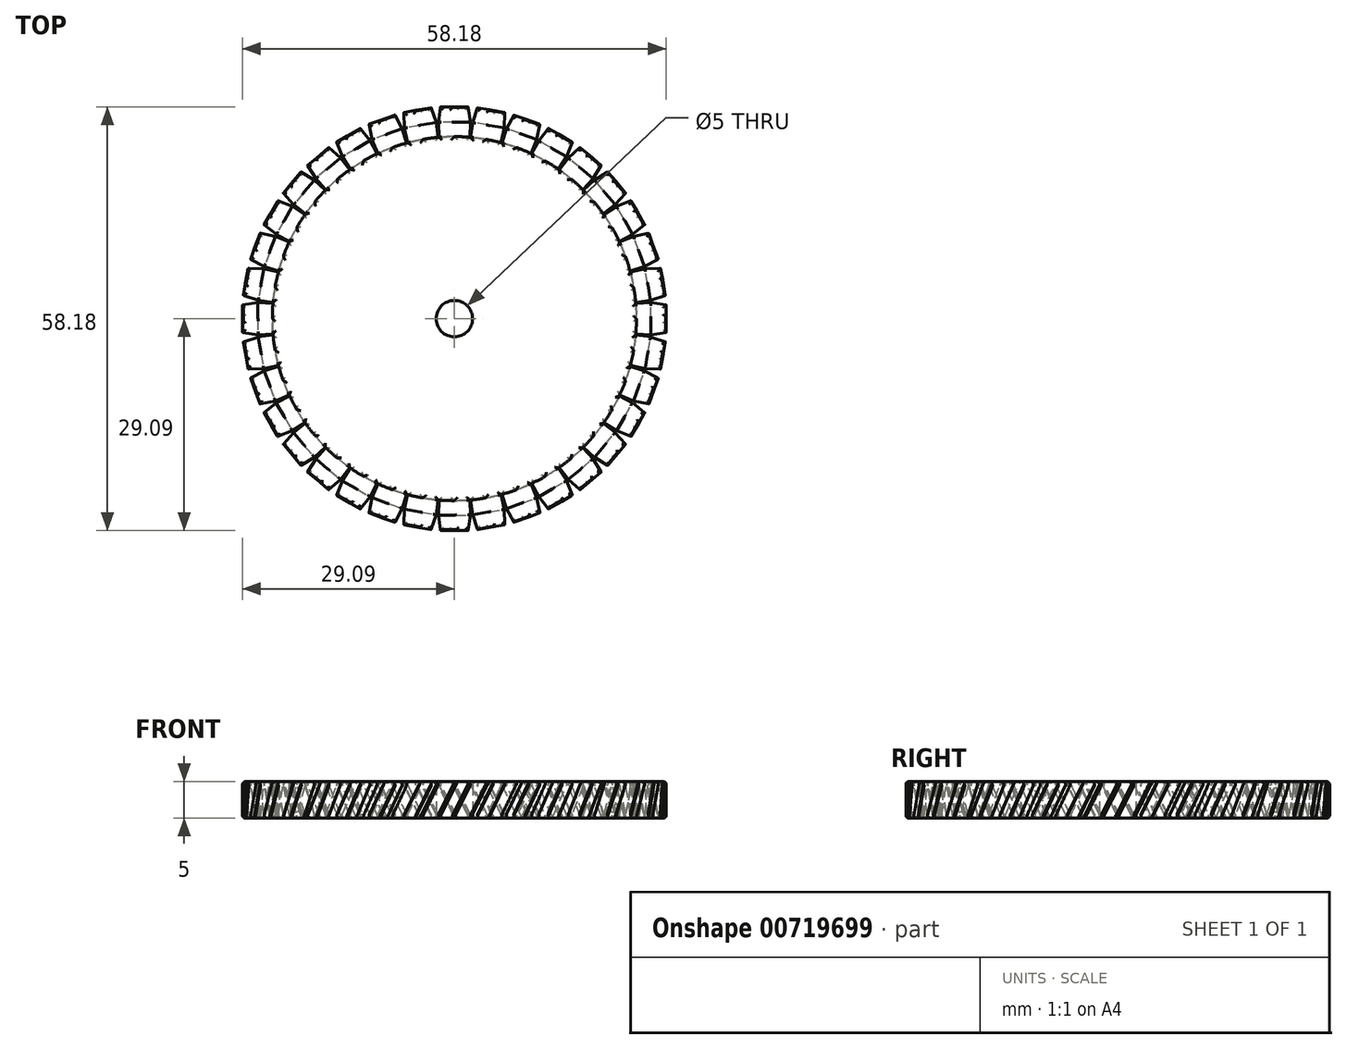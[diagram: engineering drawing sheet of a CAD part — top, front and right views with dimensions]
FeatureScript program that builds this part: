
annotation { "Feature Type Name" : "Feature", "Feature Type Description" : "" }
export const myFeature = defineFeature(function(context is Context, id is Id, definition is map)
    precondition{}
    {
        {
            var Q0;
            Q0=qCreatedBy(makeId("Top.planeOp"),FACE);
            var sketch = newSketch(context, id + "F0", { "sketchPlane" : qUnion([Q0])});
            skCircle(sketch, "E0", {"center": v(0, 0) * mm, "radius": 25 * mm});
            skCircle(sketch, "E1", {"center": v(0, 0) * mm, "radius": 2.5 * mm});
            skSolve(sketch);
        }
        {
            var Q0;
            Q0=makeQuery(id+"F0.imprint","IMPRINT",FACE,{"disambiguationData":[TD([[makeQuery(id+"F0.imprint","IMPRINT",EDGE,{"derivedFrom":sQuery(id+"F0.wireOp",EDGE,"E0")}),1.0]])]});
            extrude(context, id + "F1", {"entities" : qUnion([Q0]), "depth" : 5 * mm, "offsetDistance" : 25 * mm});
        }
        {
            var Q0;
            Q0=qCreatedBy(makeId("Top.planeOp"),FACE);
            cPlane(context, id + "F2", {"entities" : qUnion([Q0]), "cplaneType" : CPlaneType.OFFSET, "offset" : 2.5 * mm, "width" : 150 * mm, "height" : 150 * mm});
        }
        {
            var Q0;
            Q0=qCreatedBy(id+"F2.planeOp",FACE);
            var sketch = newSketch(context, id + "F3", { "sketchPlane" : qUnion([Q0])});
            skCircle(sketch, "E2", {"center": v(0, 0) * mm, "radius": 27 * mm, "construction": true});
            skCircle(sketch, "E3", {"center": v(0, 0) * mm, "radius": 29 * mm, "construction": true});
            skLineSegment(sketch, "E4", {"start": v(-1.1, 24.48) * mm, "end": v(-1.2, 26.97) * mm});
            skLineSegment(sketch, "E5", {"start": v(-1.2, 26.97) * mm, "end": v(-0.9, 28.99) * mm});
            skLineSegment(sketch, "E6", {"start": v(-0.8, 29.09) * mm, "end": v(0.8, 29.09) * mm});
            skLineSegment(sketch, "E7", {"start": v(0.9, 28.99) * mm, "end": v(1.2, 26.97) * mm});
            skLineSegment(sketch, "E8", {"start": v(1.2, 26.97) * mm, "end": v(1.1, 24.48) * mm});
            skLineSegment(sketch, "E9", {"start": v(1.1, 24.48) * mm, "end": v(-1.1, 24.48) * mm});
            skCircle(sketch, "E10", {"center": v(0, 0) * mm, "radius": 24.5 * mm, "construction": true});
            skLineSegment(sketch, "E11", {"start": v(-0.9, 28.99) * mm, "end": v(-0.8, 29.09) * mm});
            skLineSegment(sketch, "E12", {"start": v(0.8, 29.09) * mm, "end": v(0.9, 28.99) * mm});
            skSolve(sketch);
        }
        {
            var Q0;
            Q0=qCreatedBy(makeId("Front.planeOp"),FACE);
            var sketch = newSketch(context, id + "F4", { "sketchPlane" : qUnion([Q0])});
            skLineSegment(sketch, "E13", {"start": v(0, 5) * mm, "end": v(2.5, 0) * mm});
            skSolve(sketch);
        }
        {
            var Q0;
            Q0 = qSketchRegion(id + "F3", true);
            var Q1;
            Q1 = qConstructionFilter(qBodyType(qCreatedBy(id + "F4" ,EDGE), BodyType.WIRE), ConstructionObject.NO);
            sweep(context, id + "F5", {"profiles" : qUnion([Q0]), "path" : qUnion([Q1])});
        }
        {
            var Q0;
            Q0=qCreatedBy(makeId("Front.planeOp"),FACE);
            var sketch = newSketch(context, id + "F6", { "sketchPlane" : qUnion([Q0])});
            skLineSegment(sketch, "E14", {"start": v(0, 7.5) * mm, "end": v(0, -7.5) * mm, "construction": true});
            skSolve(sketch);
        }
        {
            var Q0;
            Q0=makeQuery(id+"F5.opSweep","SWEPT_BODY",BODY,{"disambiguationData":[OSD([sQuery(id+"F3.wireOp",EDGE,"E4"),sQuery(id+"F3.wireOp",EDGE,"E5"),sQuery(id+"F3.wireOp",EDGE,"E6"),sQuery(id+"F3.wireOp",EDGE,"E7"),sQuery(id+"F3.wireOp",EDGE,"E8"),sQuery(id+"F3.wireOp",EDGE,"E9"),sQuery(id+"F4.wireOp",EDGE,"E13")])]});
            var Q1;
            Q1=sQuery(id+"F6.wireOp",EDGE,"E14");
            circularPattern(context, id + "F7", {"entities" : qUnion([Q0]), "axis" : qUnion([Q1]), "angle" : 360 * degree, "instanceCount" : 36, "equalSpace" : true});
        }
        {
            var Q0;
            Q0=makeQuery(id+"F7.opPattern","COPY",BODY,{"derivedFrom":makeQuery(id+"F5.opSweep","SWEPT_BODY",BODY,{"disambiguationData":[OSD([sQuery(id+"F3.wireOp",EDGE,"E4"),sQuery(id+"F3.wireOp",EDGE,"E5"),sQuery(id+"F3.wireOp",EDGE,"E6"),sQuery(id+"F3.wireOp",EDGE,"E7"),sQuery(id+"F3.wireOp",EDGE,"E8"),sQuery(id+"F3.wireOp",EDGE,"E9"),sQuery(id+"F4.wireOp",EDGE,"E13")])]}),"instanceName":"35"});
            var Q1;
            Q1=makeQuery(id+"F7.opPattern","COPY",BODY,{"derivedFrom":makeQuery(id+"F5.opSweep","SWEPT_BODY",BODY,{"disambiguationData":[OSD([sQuery(id+"F3.wireOp",EDGE,"E4"),sQuery(id+"F3.wireOp",EDGE,"E5"),sQuery(id+"F3.wireOp",EDGE,"E6"),sQuery(id+"F3.wireOp",EDGE,"E7"),sQuery(id+"F3.wireOp",EDGE,"E8"),sQuery(id+"F3.wireOp",EDGE,"E9"),sQuery(id+"F4.wireOp",EDGE,"E13")])]}),"instanceName":"34"});
            var Q2;
            Q2=makeQuery(id+"F7.opPattern","COPY",BODY,{"derivedFrom":makeQuery(id+"F5.opSweep","SWEPT_BODY",BODY,{"disambiguationData":[OSD([sQuery(id+"F3.wireOp",EDGE,"E4"),sQuery(id+"F3.wireOp",EDGE,"E5"),sQuery(id+"F3.wireOp",EDGE,"E6"),sQuery(id+"F3.wireOp",EDGE,"E7"),sQuery(id+"F3.wireOp",EDGE,"E8"),sQuery(id+"F3.wireOp",EDGE,"E9"),sQuery(id+"F4.wireOp",EDGE,"E13")])]}),"instanceName":"25"});
            var Q3;
            Q3=makeQuery(id+"F7.opPattern","COPY",BODY,{"derivedFrom":makeQuery(id+"F5.opSweep","SWEPT_BODY",BODY,{"disambiguationData":[OSD([sQuery(id+"F3.wireOp",EDGE,"E4"),sQuery(id+"F3.wireOp",EDGE,"E5"),sQuery(id+"F3.wireOp",EDGE,"E6"),sQuery(id+"F3.wireOp",EDGE,"E7"),sQuery(id+"F3.wireOp",EDGE,"E8"),sQuery(id+"F3.wireOp",EDGE,"E9"),sQuery(id+"F4.wireOp",EDGE,"E13")])]}),"instanceName":"26"});
            var Q4;
            Q4=makeQuery(id+"F7.opPattern","COPY",BODY,{"derivedFrom":makeQuery(id+"F5.opSweep","SWEPT_BODY",BODY,{"disambiguationData":[OSD([sQuery(id+"F3.wireOp",EDGE,"E4"),sQuery(id+"F3.wireOp",EDGE,"E5"),sQuery(id+"F3.wireOp",EDGE,"E6"),sQuery(id+"F3.wireOp",EDGE,"E7"),sQuery(id+"F3.wireOp",EDGE,"E8"),sQuery(id+"F3.wireOp",EDGE,"E9"),sQuery(id+"F4.wireOp",EDGE,"E13")])]}),"instanceName":"27"});
            var Q5;
            Q5=makeQuery(id+"F7.opPattern","COPY",BODY,{"derivedFrom":makeQuery(id+"F5.opSweep","SWEPT_BODY",BODY,{"disambiguationData":[OSD([sQuery(id+"F3.wireOp",EDGE,"E4"),sQuery(id+"F3.wireOp",EDGE,"E5"),sQuery(id+"F3.wireOp",EDGE,"E6"),sQuery(id+"F3.wireOp",EDGE,"E7"),sQuery(id+"F3.wireOp",EDGE,"E8"),sQuery(id+"F3.wireOp",EDGE,"E9"),sQuery(id+"F4.wireOp",EDGE,"E13")])]}),"instanceName":"28"});
            var Q6;
            Q6=makeQuery(id+"F7.opPattern","COPY",BODY,{"derivedFrom":makeQuery(id+"F5.opSweep","SWEPT_BODY",BODY,{"disambiguationData":[OSD([sQuery(id+"F3.wireOp",EDGE,"E4"),sQuery(id+"F3.wireOp",EDGE,"E5"),sQuery(id+"F3.wireOp",EDGE,"E6"),sQuery(id+"F3.wireOp",EDGE,"E7"),sQuery(id+"F3.wireOp",EDGE,"E8"),sQuery(id+"F3.wireOp",EDGE,"E9"),sQuery(id+"F4.wireOp",EDGE,"E13")])]}),"instanceName":"29"});
            var Q7;
            Q7=makeQuery(id+"F7.opPattern","COPY",BODY,{"derivedFrom":makeQuery(id+"F5.opSweep","SWEPT_BODY",BODY,{"disambiguationData":[OSD([sQuery(id+"F3.wireOp",EDGE,"E4"),sQuery(id+"F3.wireOp",EDGE,"E5"),sQuery(id+"F3.wireOp",EDGE,"E6"),sQuery(id+"F3.wireOp",EDGE,"E7"),sQuery(id+"F3.wireOp",EDGE,"E8"),sQuery(id+"F3.wireOp",EDGE,"E9"),sQuery(id+"F4.wireOp",EDGE,"E13")])]}),"instanceName":"30"});
            var Q8;
            Q8=makeQuery(id+"F7.opPattern","COPY",BODY,{"derivedFrom":makeQuery(id+"F5.opSweep","SWEPT_BODY",BODY,{"disambiguationData":[OSD([sQuery(id+"F3.wireOp",EDGE,"E4"),sQuery(id+"F3.wireOp",EDGE,"E5"),sQuery(id+"F3.wireOp",EDGE,"E6"),sQuery(id+"F3.wireOp",EDGE,"E7"),sQuery(id+"F3.wireOp",EDGE,"E8"),sQuery(id+"F3.wireOp",EDGE,"E9"),sQuery(id+"F4.wireOp",EDGE,"E13")])]}),"instanceName":"31"});
            var Q9;
            Q9=makeQuery(id+"F7.opPattern","COPY",BODY,{"derivedFrom":makeQuery(id+"F5.opSweep","SWEPT_BODY",BODY,{"disambiguationData":[OSD([sQuery(id+"F3.wireOp",EDGE,"E4"),sQuery(id+"F3.wireOp",EDGE,"E5"),sQuery(id+"F3.wireOp",EDGE,"E6"),sQuery(id+"F3.wireOp",EDGE,"E7"),sQuery(id+"F3.wireOp",EDGE,"E8"),sQuery(id+"F3.wireOp",EDGE,"E9"),sQuery(id+"F4.wireOp",EDGE,"E13")])]}),"instanceName":"32"});
            var Q10;
            Q10=makeQuery(id+"F7.opPattern","COPY",BODY,{"derivedFrom":makeQuery(id+"F5.opSweep","SWEPT_BODY",BODY,{"disambiguationData":[OSD([sQuery(id+"F3.wireOp",EDGE,"E4"),sQuery(id+"F3.wireOp",EDGE,"E5"),sQuery(id+"F3.wireOp",EDGE,"E6"),sQuery(id+"F3.wireOp",EDGE,"E7"),sQuery(id+"F3.wireOp",EDGE,"E8"),sQuery(id+"F3.wireOp",EDGE,"E9"),sQuery(id+"F4.wireOp",EDGE,"E13")])]}),"instanceName":"33"});
            var Q11;
            Q11=makeQuery(id+"F7.opPattern","COPY",BODY,{"derivedFrom":makeQuery(id+"F5.opSweep","SWEPT_BODY",BODY,{"disambiguationData":[OSD([sQuery(id+"F3.wireOp",EDGE,"E4"),sQuery(id+"F3.wireOp",EDGE,"E5"),sQuery(id+"F3.wireOp",EDGE,"E6"),sQuery(id+"F3.wireOp",EDGE,"E7"),sQuery(id+"F3.wireOp",EDGE,"E8"),sQuery(id+"F3.wireOp",EDGE,"E9"),sQuery(id+"F4.wireOp",EDGE,"E13")])]}),"instanceName":"19"});
            var Q12;
            Q12=makeQuery(id+"F7.opPattern","COPY",BODY,{"derivedFrom":makeQuery(id+"F5.opSweep","SWEPT_BODY",BODY,{"disambiguationData":[OSD([sQuery(id+"F3.wireOp",EDGE,"E4"),sQuery(id+"F3.wireOp",EDGE,"E5"),sQuery(id+"F3.wireOp",EDGE,"E6"),sQuery(id+"F3.wireOp",EDGE,"E7"),sQuery(id+"F3.wireOp",EDGE,"E8"),sQuery(id+"F3.wireOp",EDGE,"E9"),sQuery(id+"F4.wireOp",EDGE,"E13")])]}),"instanceName":"20"});
            var Q13;
            Q13=makeQuery(id+"F7.opPattern","COPY",BODY,{"derivedFrom":makeQuery(id+"F5.opSweep","SWEPT_BODY",BODY,{"disambiguationData":[OSD([sQuery(id+"F3.wireOp",EDGE,"E4"),sQuery(id+"F3.wireOp",EDGE,"E5"),sQuery(id+"F3.wireOp",EDGE,"E6"),sQuery(id+"F3.wireOp",EDGE,"E7"),sQuery(id+"F3.wireOp",EDGE,"E8"),sQuery(id+"F3.wireOp",EDGE,"E9"),sQuery(id+"F4.wireOp",EDGE,"E13")])]}),"instanceName":"21"});
            var Q14;
            Q14=makeQuery(id+"F7.opPattern","COPY",BODY,{"derivedFrom":makeQuery(id+"F5.opSweep","SWEPT_BODY",BODY,{"disambiguationData":[OSD([sQuery(id+"F3.wireOp",EDGE,"E4"),sQuery(id+"F3.wireOp",EDGE,"E5"),sQuery(id+"F3.wireOp",EDGE,"E6"),sQuery(id+"F3.wireOp",EDGE,"E7"),sQuery(id+"F3.wireOp",EDGE,"E8"),sQuery(id+"F3.wireOp",EDGE,"E9"),sQuery(id+"F4.wireOp",EDGE,"E13")])]}),"instanceName":"22"});
            var Q15;
            Q15=makeQuery(id+"F7.opPattern","COPY",BODY,{"derivedFrom":makeQuery(id+"F5.opSweep","SWEPT_BODY",BODY,{"disambiguationData":[OSD([sQuery(id+"F3.wireOp",EDGE,"E4"),sQuery(id+"F3.wireOp",EDGE,"E5"),sQuery(id+"F3.wireOp",EDGE,"E6"),sQuery(id+"F3.wireOp",EDGE,"E7"),sQuery(id+"F3.wireOp",EDGE,"E8"),sQuery(id+"F3.wireOp",EDGE,"E9"),sQuery(id+"F4.wireOp",EDGE,"E13")])]}),"instanceName":"23"});
            var Q16;
            Q16=makeQuery(id+"F7.opPattern","COPY",BODY,{"derivedFrom":makeQuery(id+"F5.opSweep","SWEPT_BODY",BODY,{"disambiguationData":[OSD([sQuery(id+"F3.wireOp",EDGE,"E4"),sQuery(id+"F3.wireOp",EDGE,"E5"),sQuery(id+"F3.wireOp",EDGE,"E6"),sQuery(id+"F3.wireOp",EDGE,"E7"),sQuery(id+"F3.wireOp",EDGE,"E8"),sQuery(id+"F3.wireOp",EDGE,"E9"),sQuery(id+"F4.wireOp",EDGE,"E13")])]}),"instanceName":"24"});
            var Q17;
            Q17=makeQuery(id+"F7.opPattern","COPY",BODY,{"derivedFrom":makeQuery(id+"F5.opSweep","SWEPT_BODY",BODY,{"disambiguationData":[OSD([sQuery(id+"F3.wireOp",EDGE,"E4"),sQuery(id+"F3.wireOp",EDGE,"E5"),sQuery(id+"F3.wireOp",EDGE,"E6"),sQuery(id+"F3.wireOp",EDGE,"E7"),sQuery(id+"F3.wireOp",EDGE,"E8"),sQuery(id+"F3.wireOp",EDGE,"E9"),sQuery(id+"F4.wireOp",EDGE,"E13")])]}),"instanceName":"2"});
            var Q18;
            Q18=makeQuery(id+"F7.opPattern","COPY",BODY,{"derivedFrom":makeQuery(id+"F5.opSweep","SWEPT_BODY",BODY,{"disambiguationData":[OSD([sQuery(id+"F3.wireOp",EDGE,"E4"),sQuery(id+"F3.wireOp",EDGE,"E5"),sQuery(id+"F3.wireOp",EDGE,"E6"),sQuery(id+"F3.wireOp",EDGE,"E7"),sQuery(id+"F3.wireOp",EDGE,"E8"),sQuery(id+"F3.wireOp",EDGE,"E9"),sQuery(id+"F4.wireOp",EDGE,"E13")])]}),"instanceName":"3"});
            var Q19;
            Q19=makeQuery(id+"F7.opPattern","COPY",BODY,{"derivedFrom":makeQuery(id+"F5.opSweep","SWEPT_BODY",BODY,{"disambiguationData":[OSD([sQuery(id+"F3.wireOp",EDGE,"E4"),sQuery(id+"F3.wireOp",EDGE,"E5"),sQuery(id+"F3.wireOp",EDGE,"E6"),sQuery(id+"F3.wireOp",EDGE,"E7"),sQuery(id+"F3.wireOp",EDGE,"E8"),sQuery(id+"F3.wireOp",EDGE,"E9"),sQuery(id+"F4.wireOp",EDGE,"E13")])]}),"instanceName":"4"});
            var Q20;
            Q20=makeQuery(id+"F7.opPattern","COPY",BODY,{"derivedFrom":makeQuery(id+"F5.opSweep","SWEPT_BODY",BODY,{"disambiguationData":[OSD([sQuery(id+"F3.wireOp",EDGE,"E4"),sQuery(id+"F3.wireOp",EDGE,"E5"),sQuery(id+"F3.wireOp",EDGE,"E6"),sQuery(id+"F3.wireOp",EDGE,"E7"),sQuery(id+"F3.wireOp",EDGE,"E8"),sQuery(id+"F3.wireOp",EDGE,"E9"),sQuery(id+"F4.wireOp",EDGE,"E13")])]}),"instanceName":"5"});
            var Q21;
            Q21=makeQuery(id+"F7.opPattern","COPY",BODY,{"derivedFrom":makeQuery(id+"F5.opSweep","SWEPT_BODY",BODY,{"disambiguationData":[OSD([sQuery(id+"F3.wireOp",EDGE,"E4"),sQuery(id+"F3.wireOp",EDGE,"E5"),sQuery(id+"F3.wireOp",EDGE,"E6"),sQuery(id+"F3.wireOp",EDGE,"E7"),sQuery(id+"F3.wireOp",EDGE,"E8"),sQuery(id+"F3.wireOp",EDGE,"E9"),sQuery(id+"F4.wireOp",EDGE,"E13")])]}),"instanceName":"6"});
            var Q22;
            Q22=makeQuery(id+"F7.opPattern","COPY",BODY,{"derivedFrom":makeQuery(id+"F5.opSweep","SWEPT_BODY",BODY,{"disambiguationData":[OSD([sQuery(id+"F3.wireOp",EDGE,"E4"),sQuery(id+"F3.wireOp",EDGE,"E5"),sQuery(id+"F3.wireOp",EDGE,"E6"),sQuery(id+"F3.wireOp",EDGE,"E7"),sQuery(id+"F3.wireOp",EDGE,"E8"),sQuery(id+"F3.wireOp",EDGE,"E9"),sQuery(id+"F4.wireOp",EDGE,"E13")])]}),"instanceName":"7"});
            var Q23;
            Q23=makeQuery(id+"F7.opPattern","COPY",BODY,{"derivedFrom":makeQuery(id+"F5.opSweep","SWEPT_BODY",BODY,{"disambiguationData":[OSD([sQuery(id+"F3.wireOp",EDGE,"E4"),sQuery(id+"F3.wireOp",EDGE,"E5"),sQuery(id+"F3.wireOp",EDGE,"E6"),sQuery(id+"F3.wireOp",EDGE,"E7"),sQuery(id+"F3.wireOp",EDGE,"E8"),sQuery(id+"F3.wireOp",EDGE,"E9"),sQuery(id+"F4.wireOp",EDGE,"E13")])]}),"instanceName":"8"});
            var Q24;
            Q24=makeQuery(id+"F7.opPattern","COPY",BODY,{"derivedFrom":makeQuery(id+"F5.opSweep","SWEPT_BODY",BODY,{"disambiguationData":[OSD([sQuery(id+"F3.wireOp",EDGE,"E4"),sQuery(id+"F3.wireOp",EDGE,"E5"),sQuery(id+"F3.wireOp",EDGE,"E6"),sQuery(id+"F3.wireOp",EDGE,"E7"),sQuery(id+"F3.wireOp",EDGE,"E8"),sQuery(id+"F3.wireOp",EDGE,"E9"),sQuery(id+"F4.wireOp",EDGE,"E13")])]}),"instanceName":"9"});
            var Q25;
            Q25=makeQuery(id+"F7.opPattern","COPY",BODY,{"derivedFrom":makeQuery(id+"F5.opSweep","SWEPT_BODY",BODY,{"disambiguationData":[OSD([sQuery(id+"F3.wireOp",EDGE,"E4"),sQuery(id+"F3.wireOp",EDGE,"E5"),sQuery(id+"F3.wireOp",EDGE,"E6"),sQuery(id+"F3.wireOp",EDGE,"E7"),sQuery(id+"F3.wireOp",EDGE,"E8"),sQuery(id+"F3.wireOp",EDGE,"E9"),sQuery(id+"F4.wireOp",EDGE,"E13")])]}),"instanceName":"10"});
            var Q26;
            Q26=makeQuery(id+"F7.opPattern","COPY",BODY,{"derivedFrom":makeQuery(id+"F5.opSweep","SWEPT_BODY",BODY,{"disambiguationData":[OSD([sQuery(id+"F3.wireOp",EDGE,"E4"),sQuery(id+"F3.wireOp",EDGE,"E5"),sQuery(id+"F3.wireOp",EDGE,"E6"),sQuery(id+"F3.wireOp",EDGE,"E7"),sQuery(id+"F3.wireOp",EDGE,"E8"),sQuery(id+"F3.wireOp",EDGE,"E9"),sQuery(id+"F4.wireOp",EDGE,"E13")])]}),"instanceName":"11"});
            var Q27;
            Q27=makeQuery(id+"F7.opPattern","COPY",BODY,{"derivedFrom":makeQuery(id+"F5.opSweep","SWEPT_BODY",BODY,{"disambiguationData":[OSD([sQuery(id+"F3.wireOp",EDGE,"E4"),sQuery(id+"F3.wireOp",EDGE,"E5"),sQuery(id+"F3.wireOp",EDGE,"E6"),sQuery(id+"F3.wireOp",EDGE,"E7"),sQuery(id+"F3.wireOp",EDGE,"E8"),sQuery(id+"F3.wireOp",EDGE,"E9"),sQuery(id+"F4.wireOp",EDGE,"E13")])]}),"instanceName":"12"});
            var Q28;
            Q28=makeQuery(id+"F7.opPattern","COPY",BODY,{"derivedFrom":makeQuery(id+"F5.opSweep","SWEPT_BODY",BODY,{"disambiguationData":[OSD([sQuery(id+"F3.wireOp",EDGE,"E4"),sQuery(id+"F3.wireOp",EDGE,"E5"),sQuery(id+"F3.wireOp",EDGE,"E6"),sQuery(id+"F3.wireOp",EDGE,"E7"),sQuery(id+"F3.wireOp",EDGE,"E8"),sQuery(id+"F3.wireOp",EDGE,"E9"),sQuery(id+"F4.wireOp",EDGE,"E13")])]}),"instanceName":"13"});
            var Q29;
            Q29=makeQuery(id+"F7.opPattern","COPY",BODY,{"derivedFrom":makeQuery(id+"F5.opSweep","SWEPT_BODY",BODY,{"disambiguationData":[OSD([sQuery(id+"F3.wireOp",EDGE,"E4"),sQuery(id+"F3.wireOp",EDGE,"E5"),sQuery(id+"F3.wireOp",EDGE,"E6"),sQuery(id+"F3.wireOp",EDGE,"E7"),sQuery(id+"F3.wireOp",EDGE,"E8"),sQuery(id+"F3.wireOp",EDGE,"E9"),sQuery(id+"F4.wireOp",EDGE,"E13")])]}),"instanceName":"14"});
            var Q30;
            Q30=makeQuery(id+"F7.opPattern","COPY",BODY,{"derivedFrom":makeQuery(id+"F5.opSweep","SWEPT_BODY",BODY,{"disambiguationData":[OSD([sQuery(id+"F3.wireOp",EDGE,"E4"),sQuery(id+"F3.wireOp",EDGE,"E5"),sQuery(id+"F3.wireOp",EDGE,"E6"),sQuery(id+"F3.wireOp",EDGE,"E7"),sQuery(id+"F3.wireOp",EDGE,"E8"),sQuery(id+"F3.wireOp",EDGE,"E9"),sQuery(id+"F4.wireOp",EDGE,"E13")])]}),"instanceName":"15"});
            var Q31;
            Q31=makeQuery(id+"F7.opPattern","COPY",BODY,{"derivedFrom":makeQuery(id+"F5.opSweep","SWEPT_BODY",BODY,{"disambiguationData":[OSD([sQuery(id+"F3.wireOp",EDGE,"E4"),sQuery(id+"F3.wireOp",EDGE,"E5"),sQuery(id+"F3.wireOp",EDGE,"E6"),sQuery(id+"F3.wireOp",EDGE,"E7"),sQuery(id+"F3.wireOp",EDGE,"E8"),sQuery(id+"F3.wireOp",EDGE,"E9"),sQuery(id+"F4.wireOp",EDGE,"E13")])]}),"instanceName":"16"});
            var Q32;
            Q32=makeQuery(id+"F7.opPattern","COPY",BODY,{"derivedFrom":makeQuery(id+"F5.opSweep","SWEPT_BODY",BODY,{"disambiguationData":[OSD([sQuery(id+"F3.wireOp",EDGE,"E4"),sQuery(id+"F3.wireOp",EDGE,"E5"),sQuery(id+"F3.wireOp",EDGE,"E6"),sQuery(id+"F3.wireOp",EDGE,"E7"),sQuery(id+"F3.wireOp",EDGE,"E8"),sQuery(id+"F3.wireOp",EDGE,"E9"),sQuery(id+"F4.wireOp",EDGE,"E13")])]}),"instanceName":"17"});
            var Q33;
            Q33=makeQuery(id+"F7.opPattern","COPY",BODY,{"derivedFrom":makeQuery(id+"F5.opSweep","SWEPT_BODY",BODY,{"disambiguationData":[OSD([sQuery(id+"F3.wireOp",EDGE,"E4"),sQuery(id+"F3.wireOp",EDGE,"E5"),sQuery(id+"F3.wireOp",EDGE,"E6"),sQuery(id+"F3.wireOp",EDGE,"E7"),sQuery(id+"F3.wireOp",EDGE,"E8"),sQuery(id+"F3.wireOp",EDGE,"E9"),sQuery(id+"F4.wireOp",EDGE,"E13")])]}),"instanceName":"18"});
            var Q34;
            Q34=makeQuery(id+"F1.opExtrude","SWEPT_BODY",BODY,{"disambiguationData":[OSD([sQuery(id+"F0.wireOp",EDGE,"E0"),sQuery(id+"F0.wireOp",EDGE,"E1")])]});
            var Q35;
            Q35=makeQuery(id+"F5.opSweep","SWEPT_BODY",BODY,{"disambiguationData":[OSD([sQuery(id+"F3.wireOp",EDGE,"E4"),sQuery(id+"F3.wireOp",EDGE,"E5"),sQuery(id+"F3.wireOp",EDGE,"E6"),sQuery(id+"F3.wireOp",EDGE,"E7"),sQuery(id+"F3.wireOp",EDGE,"E8"),sQuery(id+"F3.wireOp",EDGE,"E9"),sQuery(id+"F4.wireOp",EDGE,"E13")])]});
            var Q36;
            Q36=makeQuery(id+"F7.opPattern","COPY",BODY,{"derivedFrom":makeQuery(id+"F5.opSweep","SWEPT_BODY",BODY,{"disambiguationData":[OSD([sQuery(id+"F3.wireOp",EDGE,"E4"),sQuery(id+"F3.wireOp",EDGE,"E5"),sQuery(id+"F3.wireOp",EDGE,"E6"),sQuery(id+"F3.wireOp",EDGE,"E7"),sQuery(id+"F3.wireOp",EDGE,"E8"),sQuery(id+"F3.wireOp",EDGE,"E9"),sQuery(id+"F4.wireOp",EDGE,"E13")])]}),"instanceName":"1"});
            booleanBodies(context, id + "F8", {"operationType" : BooleanOperationType.UNION, "tools" : qUnion([Q0, Q1, Q2, Q3, Q4, Q5, Q6, Q7, Q8, Q9, Q10, Q11, Q12, Q13, Q14, Q15, Q16, Q17, Q18, Q19, Q20, Q21, Q22, Q23, Q24, Q25, Q26, Q27, Q28, Q29, Q30, Q31, Q32, Q33, Q34, Q35, Q36])});
        }
        {
            var Q0;
            {var subQ0=makeQuery(id+"F5.opSweep","CAP_FACE",FACE,{"disambiguationData":[OSD([sQuery(id+"F3.wireOp",EDGE,"E4"),sQuery(id+"F3.wireOp",EDGE,"E5"),sQuery(id+"F3.wireOp",EDGE,"E6"),sQuery(id+"F3.wireOp",EDGE,"E7"),sQuery(id+"F3.wireOp",EDGE,"E8"),sQuery(id+"F3.wireOp",EDGE,"E9"),sQuery(id+"F4.wireOp",VERTEX,"E13.start")])],"isStart":false});Q0=makeQuery(id+"F8.opBoolean","MERGE",FACE,{"derivedFrom":[makeQuery(id+"F1.opExtrude","CAP_FACE",FACE,{"disambiguationData":[OSD([sQuery(id+"F0.wireOp",EDGE,"E0"),sQuery(id+"F0.wireOp",EDGE,"E1")])],"isStart":false}),subQ0,makeQuery(id+"F7.opPattern","COPY",FACE,{"derivedFrom":subQ0,"instanceName":"1"}),makeQuery(id+"F7.opPattern","COPY",FACE,{"derivedFrom":subQ0,"instanceName":"2"}),makeQuery(id+"F7.opPattern","COPY",FACE,{"derivedFrom":subQ0,"instanceName":"3"}),makeQuery(id+"F7.opPattern","COPY",FACE,{"derivedFrom":subQ0,"instanceName":"4"}),makeQuery(id+"F7.opPattern","COPY",FACE,{"derivedFrom":subQ0,"instanceName":"5"}),makeQuery(id+"F7.opPattern","COPY",FACE,{"derivedFrom":subQ0,"instanceName":"6"}),makeQuery(id+"F7.opPattern","COPY",FACE,{"derivedFrom":subQ0,"instanceName":"7"}),makeQuery(id+"F7.opPattern","COPY",FACE,{"derivedFrom":subQ0,"instanceName":"8"}),makeQuery(id+"F7.opPattern","COPY",FACE,{"derivedFrom":subQ0,"instanceName":"9"}),makeQuery(id+"F7.opPattern","COPY",FACE,{"derivedFrom":subQ0,"instanceName":"10"}),makeQuery(id+"F7.opPattern","COPY",FACE,{"derivedFrom":subQ0,"instanceName":"11"}),makeQuery(id+"F7.opPattern","COPY",FACE,{"derivedFrom":subQ0,"instanceName":"12"}),makeQuery(id+"F7.opPattern","COPY",FACE,{"derivedFrom":subQ0,"instanceName":"13"}),makeQuery(id+"F7.opPattern","COPY",FACE,{"derivedFrom":subQ0,"instanceName":"14"}),makeQuery(id+"F7.opPattern","COPY",FACE,{"derivedFrom":subQ0,"instanceName":"15"}),makeQuery(id+"F7.opPattern","COPY",FACE,{"derivedFrom":subQ0,"instanceName":"16"}),makeQuery(id+"F7.opPattern","COPY",FACE,{"derivedFrom":subQ0,"instanceName":"17"}),makeQuery(id+"F7.opPattern","COPY",FACE,{"derivedFrom":subQ0,"instanceName":"18"}),makeQuery(id+"F7.opPattern","COPY",FACE,{"derivedFrom":subQ0,"instanceName":"19"}),makeQuery(id+"F7.opPattern","COPY",FACE,{"derivedFrom":subQ0,"instanceName":"20"}),makeQuery(id+"F7.opPattern","COPY",FACE,{"derivedFrom":subQ0,"instanceName":"21"}),makeQuery(id+"F7.opPattern","COPY",FACE,{"derivedFrom":subQ0,"instanceName":"22"}),makeQuery(id+"F7.opPattern","COPY",FACE,{"derivedFrom":subQ0,"instanceName":"23"}),makeQuery(id+"F7.opPattern","COPY",FACE,{"derivedFrom":subQ0,"instanceName":"24"}),makeQuery(id+"F7.opPattern","COPY",FACE,{"derivedFrom":subQ0,"instanceName":"25"}),makeQuery(id+"F7.opPattern","COPY",FACE,{"derivedFrom":subQ0,"instanceName":"26"}),makeQuery(id+"F7.opPattern","COPY",FACE,{"derivedFrom":subQ0,"instanceName":"27"}),makeQuery(id+"F7.opPattern","COPY",FACE,{"derivedFrom":subQ0,"instanceName":"28"}),makeQuery(id+"F7.opPattern","COPY",FACE,{"derivedFrom":subQ0,"instanceName":"29"}),makeQuery(id+"F7.opPattern","COPY",FACE,{"derivedFrom":subQ0,"instanceName":"30"}),makeQuery(id+"F7.opPattern","COPY",FACE,{"derivedFrom":subQ0,"instanceName":"31"}),makeQuery(id+"F7.opPattern","COPY",FACE,{"derivedFrom":subQ0,"instanceName":"32"}),makeQuery(id+"F7.opPattern","COPY",FACE,{"derivedFrom":subQ0,"instanceName":"33"}),makeQuery(id+"F7.opPattern","COPY",FACE,{"derivedFrom":subQ0,"instanceName":"34"}),makeQuery(id+"F7.opPattern","COPY",FACE,{"derivedFrom":subQ0,"instanceName":"35"})]});}
            var Q1;
            {var subQ0=makeQuery(id+"F5.opSweep","CAP_FACE",FACE,{"disambiguationData":[OSD([sQuery(id+"F3.wireOp",EDGE,"E4"),sQuery(id+"F3.wireOp",EDGE,"E5"),sQuery(id+"F3.wireOp",EDGE,"E6"),sQuery(id+"F3.wireOp",EDGE,"E7"),sQuery(id+"F3.wireOp",EDGE,"E8"),sQuery(id+"F3.wireOp",EDGE,"E9"),sQuery(id+"F4.wireOp",VERTEX,"E13.end")])],"isStart":true});Q1=makeQuery(id+"F8.opBoolean","MERGE",FACE,{"derivedFrom":[makeQuery(id+"F1.opExtrude","CAP_FACE",FACE,{"disambiguationData":[OSD([sQuery(id+"F0.wireOp",EDGE,"E0"),sQuery(id+"F0.wireOp",EDGE,"E1")])],"isStart":true}),subQ0,makeQuery(id+"F7.opPattern","COPY",FACE,{"derivedFrom":subQ0,"instanceName":"1"}),makeQuery(id+"F7.opPattern","COPY",FACE,{"derivedFrom":subQ0,"instanceName":"2"}),makeQuery(id+"F7.opPattern","COPY",FACE,{"derivedFrom":subQ0,"instanceName":"3"}),makeQuery(id+"F7.opPattern","COPY",FACE,{"derivedFrom":subQ0,"instanceName":"4"}),makeQuery(id+"F7.opPattern","COPY",FACE,{"derivedFrom":subQ0,"instanceName":"5"}),makeQuery(id+"F7.opPattern","COPY",FACE,{"derivedFrom":subQ0,"instanceName":"6"}),makeQuery(id+"F7.opPattern","COPY",FACE,{"derivedFrom":subQ0,"instanceName":"7"}),makeQuery(id+"F7.opPattern","COPY",FACE,{"derivedFrom":subQ0,"instanceName":"8"}),makeQuery(id+"F7.opPattern","COPY",FACE,{"derivedFrom":subQ0,"instanceName":"9"}),makeQuery(id+"F7.opPattern","COPY",FACE,{"derivedFrom":subQ0,"instanceName":"10"}),makeQuery(id+"F7.opPattern","COPY",FACE,{"derivedFrom":subQ0,"instanceName":"11"}),makeQuery(id+"F7.opPattern","COPY",FACE,{"derivedFrom":subQ0,"instanceName":"12"}),makeQuery(id+"F7.opPattern","COPY",FACE,{"derivedFrom":subQ0,"instanceName":"13"}),makeQuery(id+"F7.opPattern","COPY",FACE,{"derivedFrom":subQ0,"instanceName":"14"}),makeQuery(id+"F7.opPattern","COPY",FACE,{"derivedFrom":subQ0,"instanceName":"15"}),makeQuery(id+"F7.opPattern","COPY",FACE,{"derivedFrom":subQ0,"instanceName":"16"}),makeQuery(id+"F7.opPattern","COPY",FACE,{"derivedFrom":subQ0,"instanceName":"17"}),makeQuery(id+"F7.opPattern","COPY",FACE,{"derivedFrom":subQ0,"instanceName":"18"}),makeQuery(id+"F7.opPattern","COPY",FACE,{"derivedFrom":subQ0,"instanceName":"19"}),makeQuery(id+"F7.opPattern","COPY",FACE,{"derivedFrom":subQ0,"instanceName":"20"}),makeQuery(id+"F7.opPattern","COPY",FACE,{"derivedFrom":subQ0,"instanceName":"21"}),makeQuery(id+"F7.opPattern","COPY",FACE,{"derivedFrom":subQ0,"instanceName":"22"}),makeQuery(id+"F7.opPattern","COPY",FACE,{"derivedFrom":subQ0,"instanceName":"23"}),makeQuery(id+"F7.opPattern","COPY",FACE,{"derivedFrom":subQ0,"instanceName":"24"}),makeQuery(id+"F7.opPattern","COPY",FACE,{"derivedFrom":subQ0,"instanceName":"25"}),makeQuery(id+"F7.opPattern","COPY",FACE,{"derivedFrom":subQ0,"instanceName":"26"}),makeQuery(id+"F7.opPattern","COPY",FACE,{"derivedFrom":subQ0,"instanceName":"27"}),makeQuery(id+"F7.opPattern","COPY",FACE,{"derivedFrom":subQ0,"instanceName":"28"}),makeQuery(id+"F7.opPattern","COPY",FACE,{"derivedFrom":subQ0,"instanceName":"29"}),makeQuery(id+"F7.opPattern","COPY",FACE,{"derivedFrom":subQ0,"instanceName":"30"}),makeQuery(id+"F7.opPattern","COPY",FACE,{"derivedFrom":subQ0,"instanceName":"31"}),makeQuery(id+"F7.opPattern","COPY",FACE,{"derivedFrom":subQ0,"instanceName":"32"}),makeQuery(id+"F7.opPattern","COPY",FACE,{"derivedFrom":subQ0,"instanceName":"33"}),makeQuery(id+"F7.opPattern","COPY",FACE,{"derivedFrom":subQ0,"instanceName":"34"}),makeQuery(id+"F7.opPattern","COPY",FACE,{"derivedFrom":subQ0,"instanceName":"35"})]});}
            fillet(context, id + "F9", {"entities" : qUnion([Q0, Q1]), "radius" : 0.4 * mm, "tangentPropagation" : true, "allowEdgeOverflow" : false});
        }
    });
